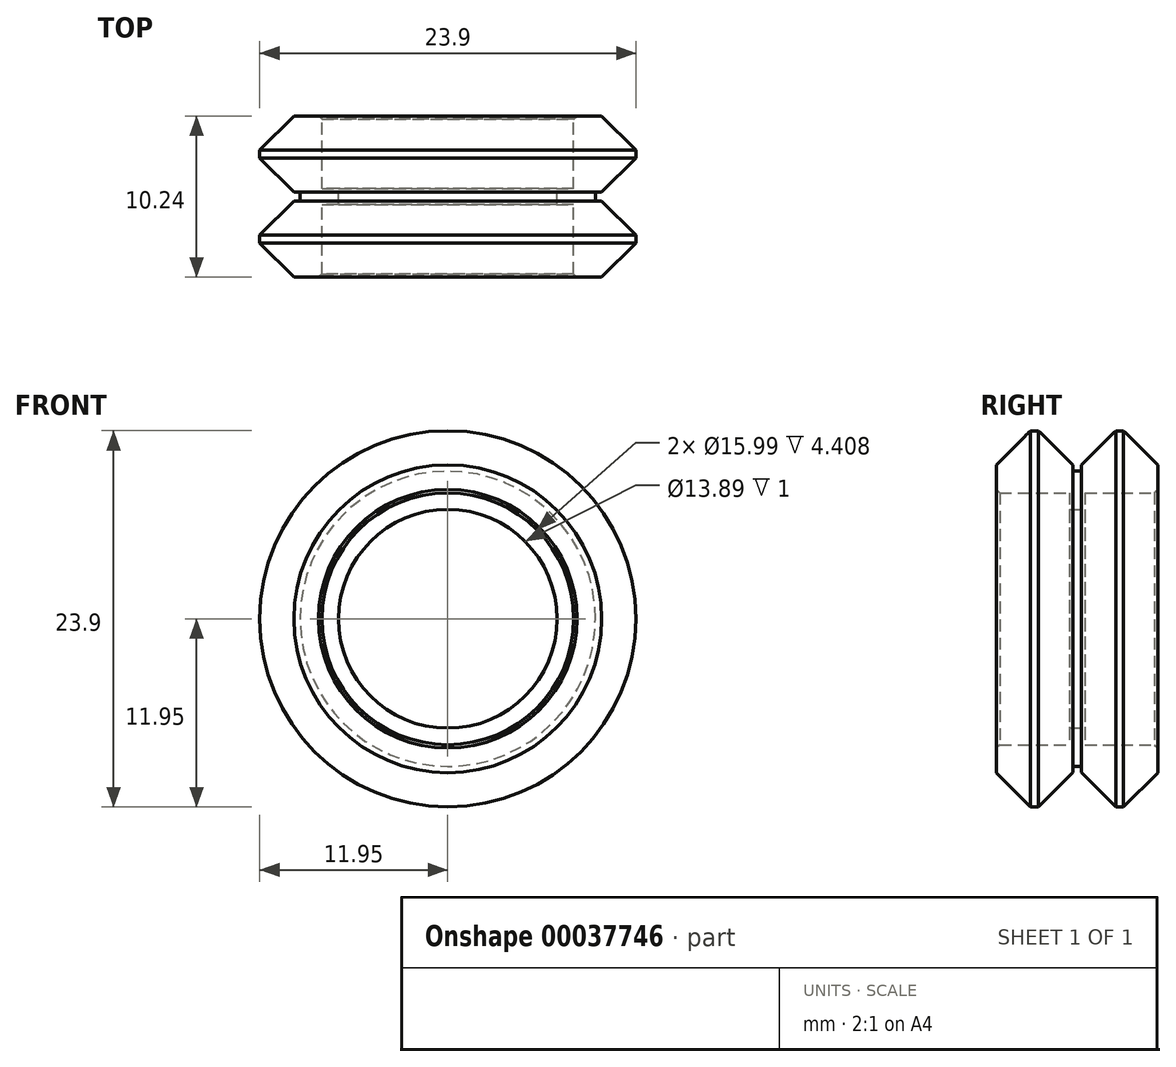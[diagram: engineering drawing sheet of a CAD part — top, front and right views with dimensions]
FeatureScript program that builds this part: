
annotation { "Feature Type Name" : "Feature", "Feature Type Description" : "" }
export const myFeature = defineFeature(function(context is Context, id is Id, definition is map)
    precondition{}
    {
        {
            var Q0;
            Q0=qCreatedBy(makeId("Right.planeOp"),FACE);
            var sketch = newSketch(context, id + "F0", { "sketchPlane" : qUnion([Q0])});
            skLineSegment(sketch, "E0", {"start": v(-0.5, 6.94) * mm, "end": v(-0.5, 8) * mm});
            skLineSegment(sketch, "E1", {"start": v(-0.5, 8) * mm, "end": v(-4.9, 8) * mm});
            skLineSegment(sketch, "E2", {"start": v(-4.9, 8) * mm, "end": v(-5.12, 8.2) * mm});
            skLineSegment(sketch, "E3", {"start": v(-5.12, 8.2) * mm, "end": v(-5.12, 9.78) * mm});
            skLineSegment(sketch, "E4", {"start": v(-5.12, 9.78) * mm, "end": v(-2.95, 11.95) * mm});
            skLineSegment(sketch, "E5", {"start": v(-2.45, 11.95) * mm, "end": v(-0.27, 9.77) * mm});
            skLineSegment(sketch, "E6", {"start": v(9.99, 0) * mm, "end": v(-9.48, 0) * mm, "construction": true});
            skLineSegment(sketch, "E7", {"start": v(-0.5, 6.94) * mm, "end": v(0.5, 6.94) * mm});
            skLineSegment(sketch, "E8", {"start": v(-0.28, 9.77) * mm, "end": v(-0.28, 9.38) * mm});
            skLineSegment(sketch, "E9", {"start": v(-0.27, 9.38) * mm, "end": v(0, 9.38) * mm});
            skLineSegment(sketch, "E10", {"start": v(0, 9.38) * mm, "end": v(0.27, 9.38) * mm});
            skLineSegment(sketch, "E11", {"start": v(0.28, 9.38) * mm, "end": v(0.28, 9.77) * mm});
            skLineSegment(sketch, "E12", {"start": v(0.27, 9.77) * mm, "end": v(2.45, 11.94) * mm});
            skLineSegment(sketch, "E13", {"start": v(2.95, 11.95) * mm, "end": v(5.12, 9.78) * mm});
            skLineSegment(sketch, "E14", {"start": v(5.12, 9.78) * mm, "end": v(5.12, 8.2) * mm});
            skLineSegment(sketch, "E15", {"start": v(5.12, 8.2) * mm, "end": v(4.9, 8) * mm});
            skLineSegment(sketch, "E16", {"start": v(4.9, 8) * mm, "end": v(0.5, 8) * mm});
            skLineSegment(sketch, "E17", {"start": v(0.5, 8) * mm, "end": v(0.5, 6.94) * mm});
            skLineSegment(sketch, "E18", {"start": v(-2.95, 11.95) * mm, "end": v(-2.45, 11.95) * mm});
            skPoint(sketch, "E19.orphan", {"position": v(-2.7, 12.2) * mm});
            skPoint(sketch, "E20.orphan", {"position": v(2.7, 12.2) * mm});
            skLineSegment(sketch, "E21.trimOffspring", {"start": v(2.45, 11.95) * mm, "end": v(2.95, 11.95) * mm});
            skSolve(sketch);
        }
        {
            var Q0;
            Q0 = qSketchRegion(id + "F0", true);
            var Q1;
            Q1=sQuery(id+"F0.wireOp",EDGE,"E6");
            revolve(context, id + "F1", {"entities" : qUnion([Q0]), "axis" : qUnion([Q1]), "revolveType" : RevolveType.FULL});
        }
    });
